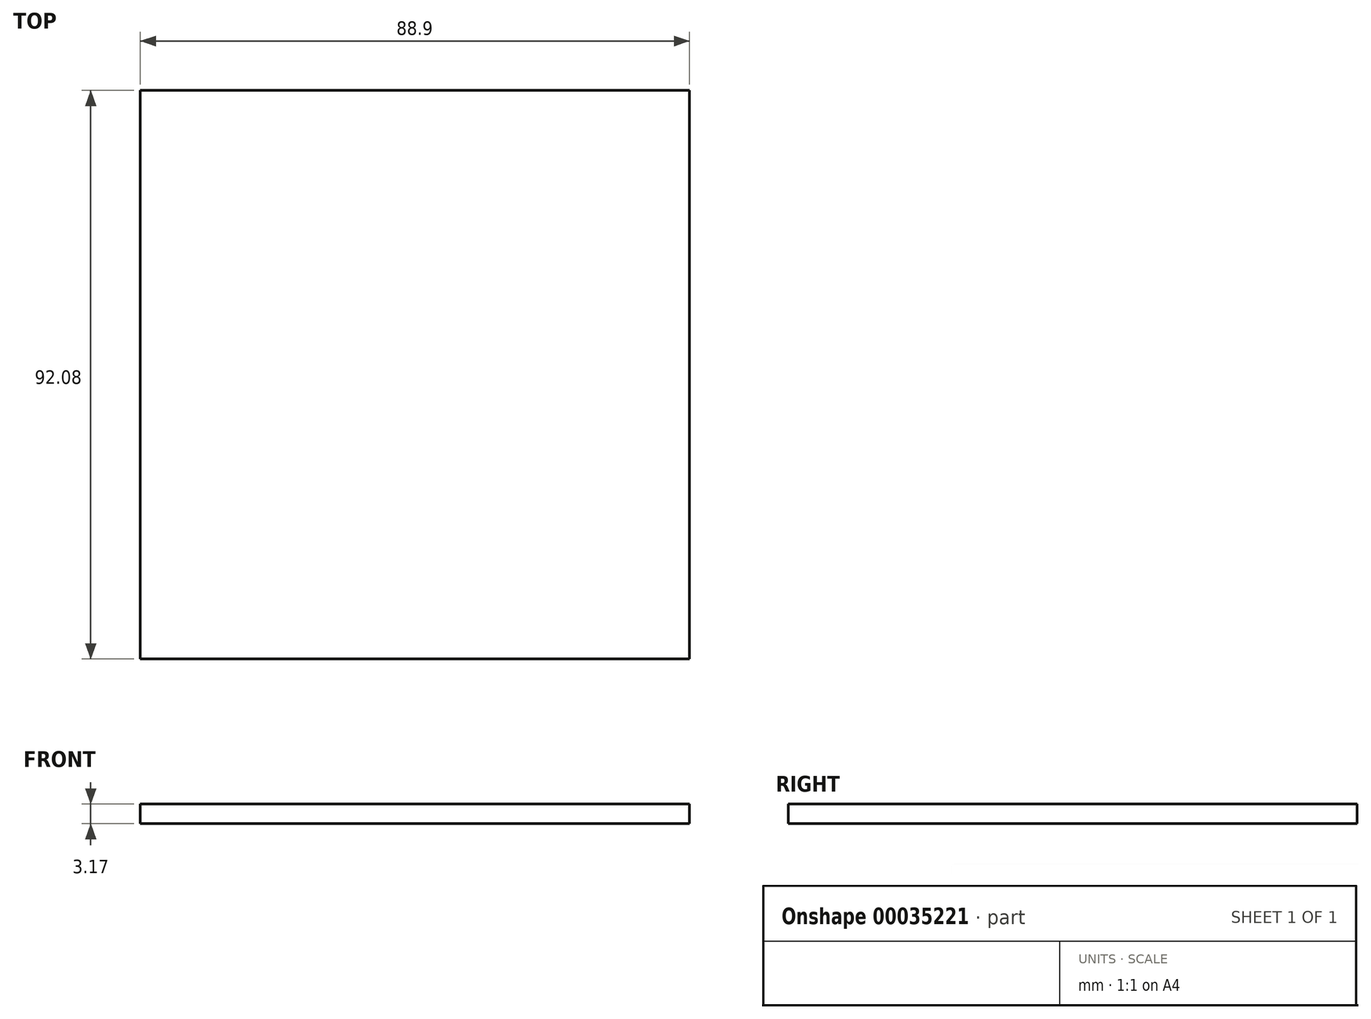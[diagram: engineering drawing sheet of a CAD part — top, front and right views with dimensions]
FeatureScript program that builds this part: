
annotation { "Feature Type Name" : "Feature", "Feature Type Description" : "" }
export const myFeature = defineFeature(function(context is Context, id is Id, definition is map)
    precondition{}
    {
        {
            var Q0;
            Q0=qCreatedBy(makeId("Top.planeOp"),FACE);
            var sketch = newSketch(context, id + "F0", { "sketchPlane" : qUnion([Q0])});
            skLineSegment(sketch, "E0.rect.bottom", {"start": v(44.45, 46.04) * mm, "end": v(-44.45, 46.04) * mm});
            skLineSegment(sketch, "E0.rect.top", {"start": v(44.45, -46.04) * mm, "end": v(-44.45, -46.04) * mm});
            skLineSegment(sketch, "E0.rect.left", {"start": v(44.45, 46.04) * mm, "end": v(44.45, -46.04) * mm});
            skLineSegment(sketch, "E0.rect.right", {"start": v(-44.45, 46.04) * mm, "end": v(-44.45, -46.04) * mm});
            skPoint(sketch, "E0.rect.middle", {"position": v(0, 0) * mm});
            skSolve(sketch);
        }
        {
            var Q0;
            Q0=makeQuery(id+"F0.imprint","IMPRINT",FACE,{"disambiguationData":[TD([[makeQuery(id+"F0.imprint","IMPRINT",EDGE,{"derivedFrom":sQuery(id+"F0.wireOp",EDGE,"E0.rect.bottom")}),1.0]])]});
            extrude(context, id + "F1", {"entities" : qUnion([Q0]), "depth" : 3.17 * mm});
        }
    });
